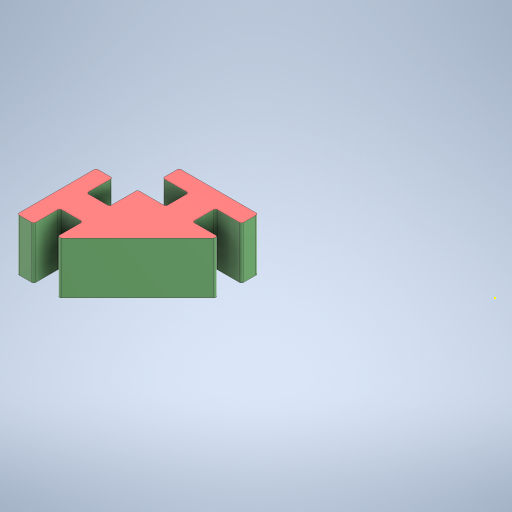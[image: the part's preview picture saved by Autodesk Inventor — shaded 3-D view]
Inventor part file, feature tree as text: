
AUTODESK INVENTOR PART (.ipt)
format: ipt  version: 2023 (Build 270158000, 158)  size: 285,696 bytes
history: native  units: in
note: dims shown in document units (in); Inventor stores cm internally (conversion verified against a paired STEP export)
features: other x4, sketch x1
ambient origin geometry x8: Origin, YZ Plane, XZ Plane, XY Plane, X Axis, Y Axis, Z Axis, Center Point
bodies: Body1 (feature_tree)
feature tree (5):
  other  "FlexPart.ipt"
  sketch  "Sketch1"  dims[d0=0.3937in]
  other  "PLA2::FlexPart.ipt"
  other  "TaggingFeature1"
  other  "PLA2"
